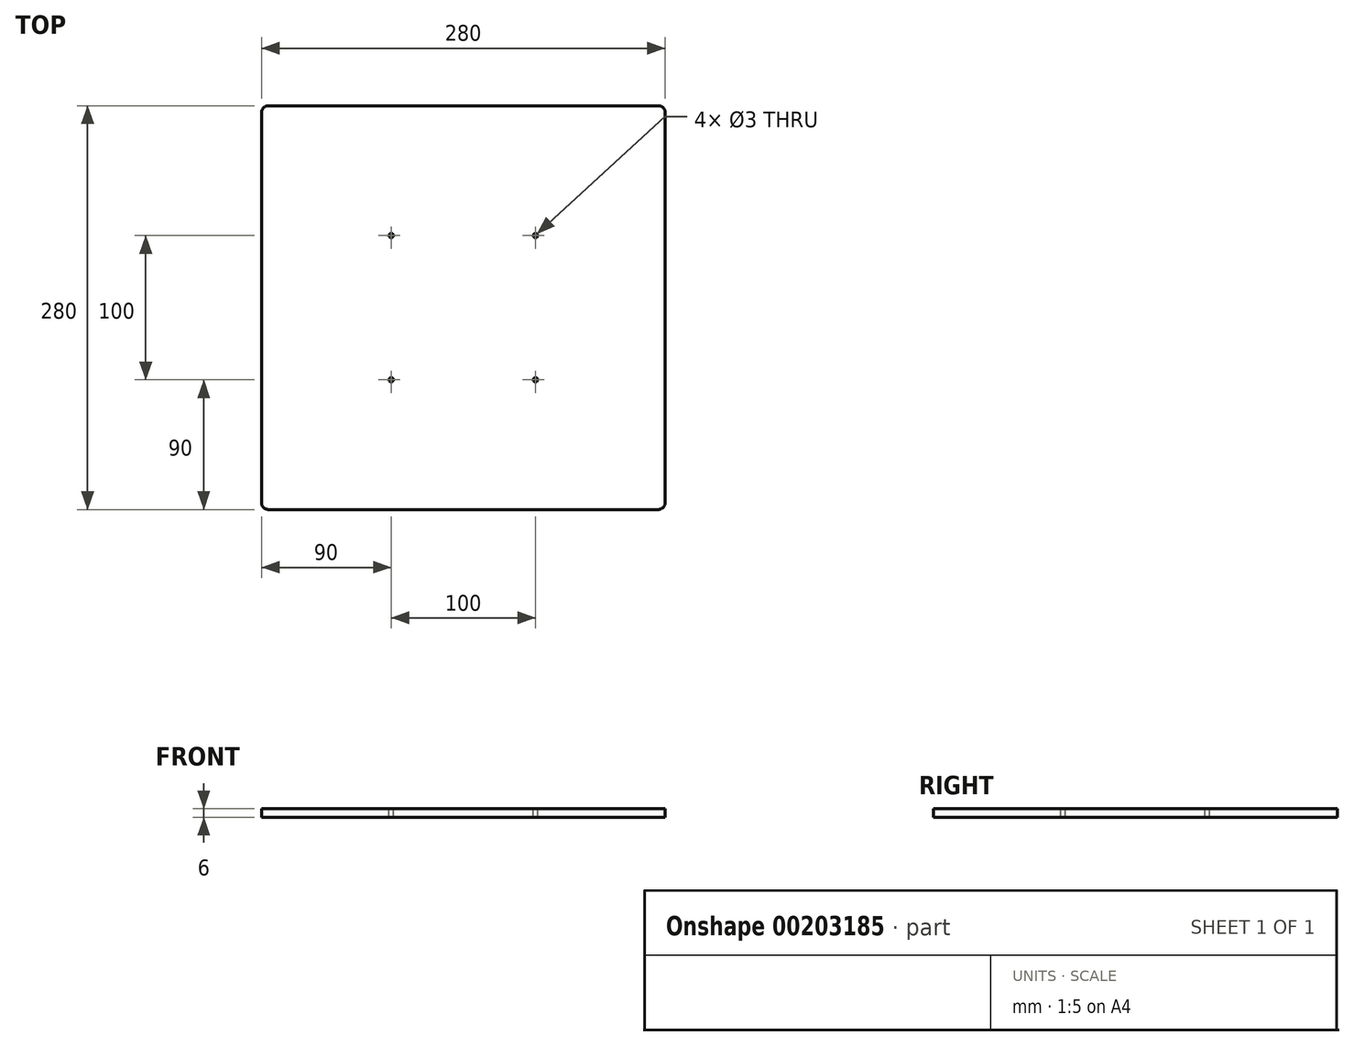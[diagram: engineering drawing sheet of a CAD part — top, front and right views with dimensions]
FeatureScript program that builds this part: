
annotation { "Feature Type Name" : "Feature", "Feature Type Description" : "" }
export const myFeature = defineFeature(function(context is Context, id is Id, definition is map)
    precondition{}
    {
        {
            var Q0;
            Q0=qCreatedBy(makeId("Top.planeOp"),FACE);
            var sketch = newSketch(context, id + "F0", { "sketchPlane" : qUnion([Q0])});
            skLineSegment(sketch, "E0.bottom", {"start": v(135, -140) * mm, "end": v(-135, -140) * mm});
            skLineSegment(sketch, "E0.top", {"start": v(135, 140) * mm, "end": v(-135, 140) * mm});
            skLineSegment(sketch, "E0.left", {"start": v(140, -135) * mm, "end": v(140, 135) * mm});
            skLineSegment(sketch, "E0.right", {"start": v(-140, -135) * mm, "end": v(-140, 135) * mm});
            skPoint(sketch, "E0.middle", {"position": v(0, 0) * mm});
            skPoint(sketch, "E1.visualSharp", {"position": v(-140, 140) * mm});
            skArc(sketch, "E1.filletArc", {"start": v(-135, 140) * mm, "mid": v(-138.54, 138.54) * mm, "end": v(-140, 135) * mm});
            skPoint(sketch, "E2.visualSharp", {"position": v(140, 140) * mm});
            skArc(sketch, "E2.filletArc", {"start": v(140, 135) * mm, "mid": v(138.54, 138.54) * mm, "end": v(135, 140) * mm});
            skPoint(sketch, "E3.visualSharp", {"position": v(140, -140) * mm});
            skArc(sketch, "E3.filletArc", {"start": v(135, -140) * mm, "mid": v(138.54, -138.54) * mm, "end": v(140, -135) * mm});
            skPoint(sketch, "E4.visualSharp", {"position": v(-140, -140) * mm});
            skArc(sketch, "E4.filletArc", {"start": v(-140, -135) * mm, "mid": v(-138.54, -138.54) * mm, "end": v(-135, -140) * mm});
            skSolve(sketch);
        }
        {
            var Q0;
            Q0 = qSketchRegion(id + "F0", true);
            extrude(context, id + "F1", {"entities" : qUnion([Q0]), "depth" : 6 * mm});
        }
        {
            var Q0;
            Q0=makeQuery(id+"F1.opExtrude","CAP_FACE",FACE,{"disambiguationData":[OSD([sQuery(id+"F0.wireOp",EDGE,"E0.bottom"),sQuery(id+"F0.wireOp",EDGE,"E0.top"),sQuery(id+"F0.wireOp",EDGE,"E0.left"),sQuery(id+"F0.wireOp",EDGE,"E0.right"),sQuery(id+"F0.wireOp",EDGE,"E1.filletArc"),sQuery(id+"F0.wireOp",EDGE,"E2.filletArc"),sQuery(id+"F0.wireOp",EDGE,"E3.filletArc"),sQuery(id+"F0.wireOp",EDGE,"E4.filletArc")])],"isStart":false});
            var sketch = newSketch(context, id + "F2", { "sketchPlane" : qUnion([Q0])});
            skLineSegment(sketch, "E5.bottom", {"start": v(50, -50) * mm, "end": v(-50, -50) * mm, "construction": true});
            skLineSegment(sketch, "E5.top", {"start": v(50, 50) * mm, "end": v(-50, 50) * mm, "construction": true});
            skLineSegment(sketch, "E5.left", {"start": v(50, -50) * mm, "end": v(50, 50) * mm, "construction": true});
            skLineSegment(sketch, "E5.right", {"start": v(-50, -50) * mm, "end": v(-50, 50) * mm, "construction": true});
            skPoint(sketch, "E5.middle", {"position": v(0, 0) * mm});
            skCircle(sketch, "E6", {"center": v(-50, 50) * mm, "radius": 1.5 * mm});
            skCircle(sketch, "E7", {"center": v(50, 50) * mm, "radius": 1.5 * mm});
            skCircle(sketch, "E8", {"center": v(50, -50) * mm, "radius": 1.5 * mm});
            skCircle(sketch, "E9", {"center": v(-50, -50) * mm, "radius": 1.5 * mm});
            skSolve(sketch);
        }
        {
            var Q0;
            Q0 = qSketchRegion(id + "F2", true);
            extrude(context, id + "F3", {"entities" : qUnion([Q0]), "operationType" : NewBodyOperationType.REMOVE, "endBound" : BoundingType.UP_TO_NEXT, "oppositeDirection" : true, "depth" : 25 * mm});
        }
    });
